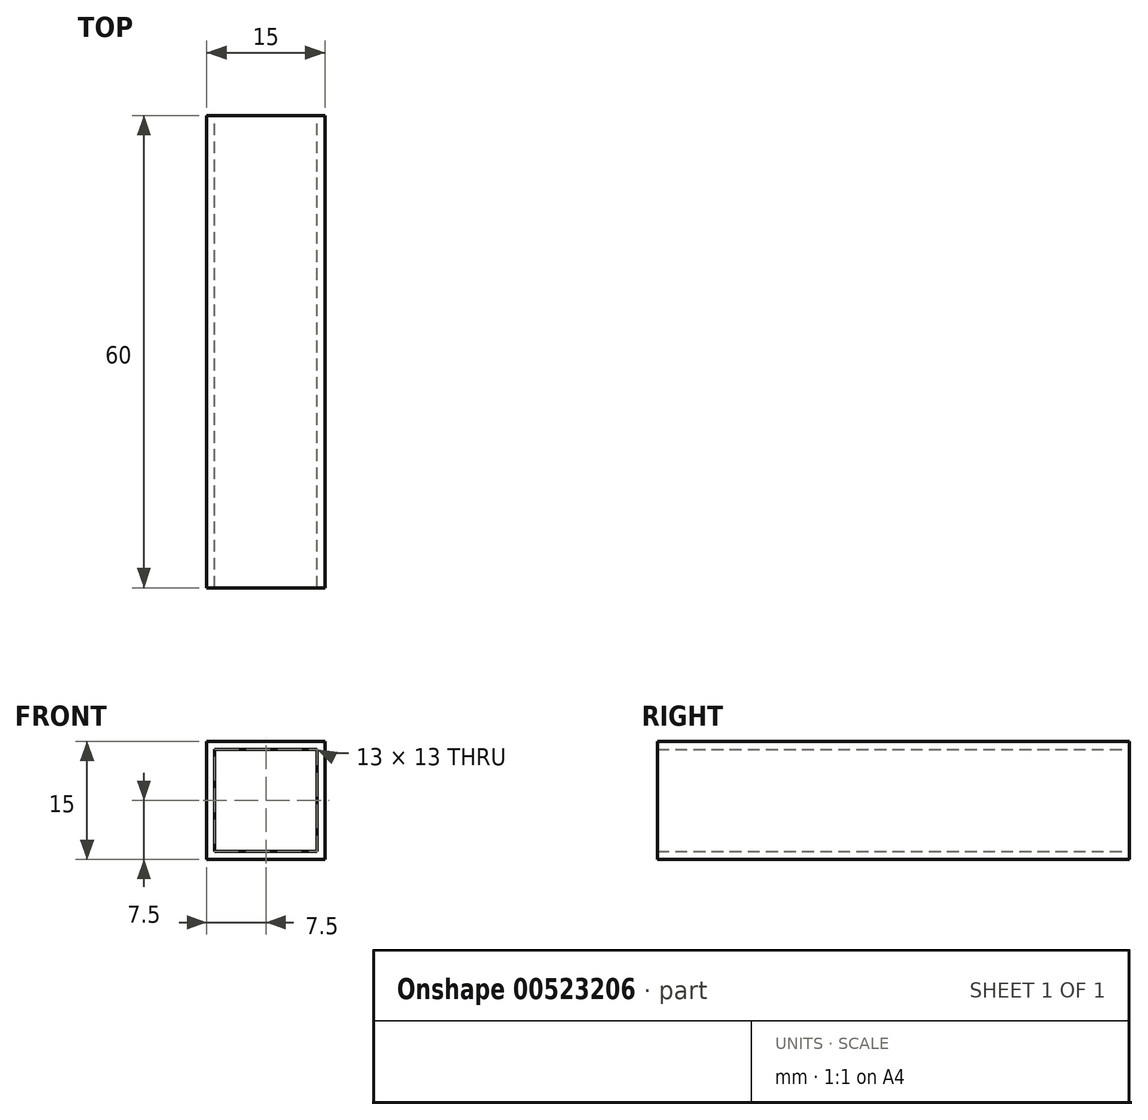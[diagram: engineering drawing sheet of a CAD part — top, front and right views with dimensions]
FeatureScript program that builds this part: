
annotation { "Feature Type Name" : "Feature", "Feature Type Description" : "" }
export const myFeature = defineFeature(function(context is Context, id is Id, definition is map)
    precondition{}
    {
        {
            var Q0;
            Q0=qCreatedBy(makeId("Front.planeOp"),FACE);
            var sketch = newSketch(context, id + "F0", { "sketchPlane" : qUnion([Q0])});
            skLineSegment(sketch, "E0.bottom", {"start": v(7.5, 7.5) * mm, "end": v(-7.5, 7.5) * mm});
            skLineSegment(sketch, "E0.top", {"start": v(7.5, -7.5) * mm, "end": v(-7.5, -7.5) * mm});
            skLineSegment(sketch, "E0.left", {"start": v(7.5, 7.5) * mm, "end": v(7.5, -7.5) * mm});
            skLineSegment(sketch, "E0.right", {"start": v(-7.5, 7.5) * mm, "end": v(-7.5, -7.5) * mm});
            skPoint(sketch, "E0.middle", {"position": v(0, 0) * mm});
            skLineSegment(sketch, "E1.0", {"start": v(-6.5, 6.5) * mm, "end": v(-6.5, -6.5) * mm});
            skLineSegment(sketch, "E1.1", {"start": v(6.5, 6.5) * mm, "end": v(-6.5, 6.5) * mm});
            skLineSegment(sketch, "E1.2", {"start": v(6.5, 6.5) * mm, "end": v(6.5, -6.5) * mm});
            skLineSegment(sketch, "E1.3", {"start": v(6.5, -6.5) * mm, "end": v(-6.5, -6.5) * mm});
            skSolve(sketch);
        }
        {
            var Q0;
            Q0=makeQuery(id+"F0.imprint","IMPRINT",FACE,{"disambiguationData":[TD([[makeQuery(id+"F0.imprint","IMPRINT",EDGE,{"derivedFrom":sQuery(id+"F0.wireOp",EDGE,"E0.bottom")}),1.0]])]});
            extrude(context, id + "F1", {"entities" : qUnion([Q0]), "depth" : 60 * mm, "offsetDistance" : 25 * mm});
        }
    });
